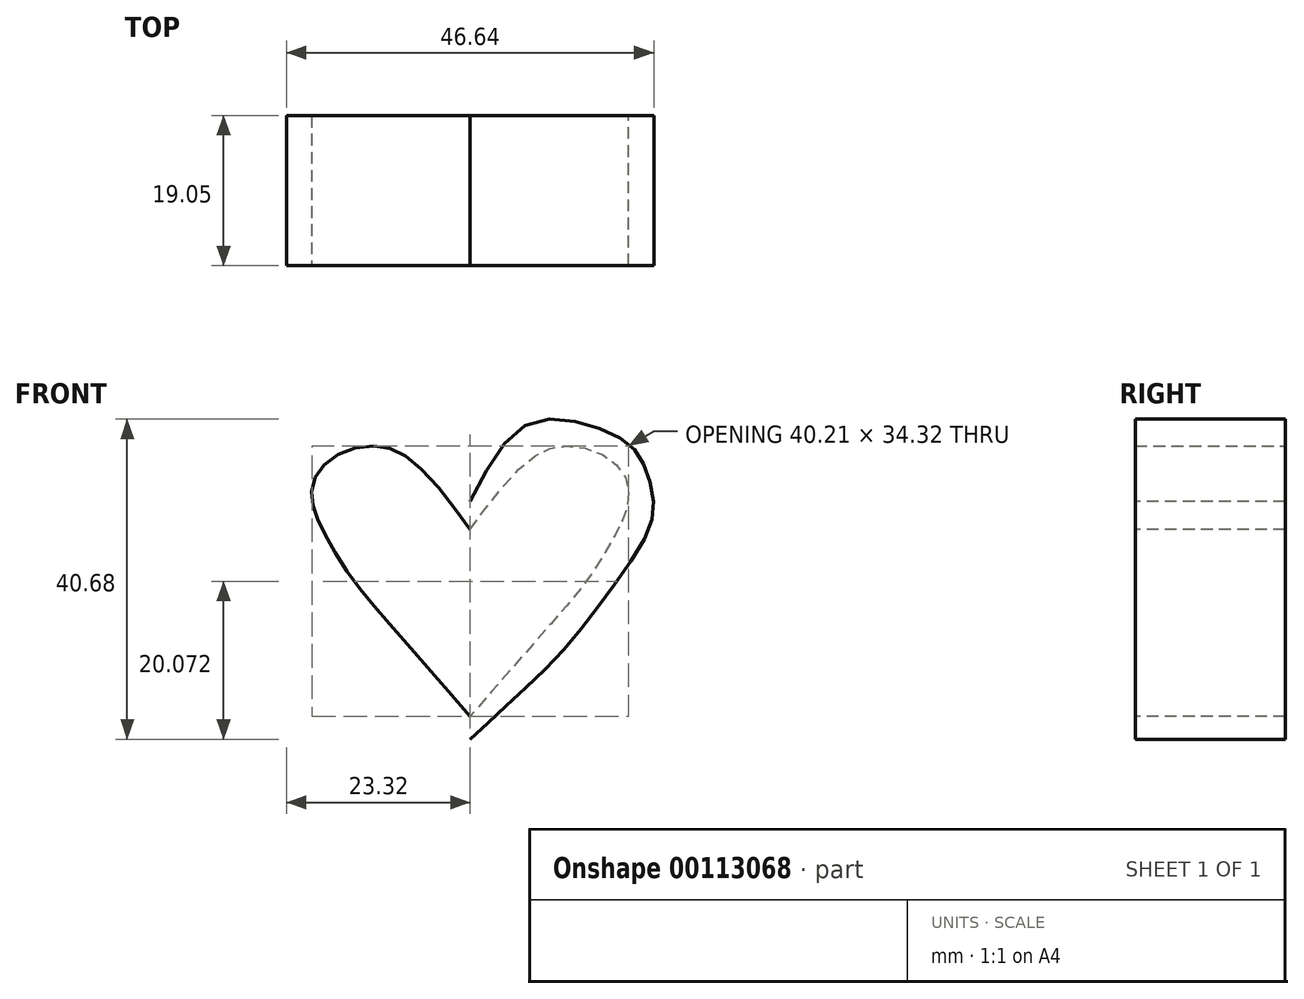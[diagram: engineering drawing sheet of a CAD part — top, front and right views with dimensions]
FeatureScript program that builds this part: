
annotation { "Feature Type Name" : "Feature", "Feature Type Description" : "" }
export const myFeature = defineFeature(function(context is Context, id is Id, definition is map)
    precondition{}
    {
        {
            var Q0;
            Q0=qCreatedBy(makeId("Front.planeOp"),FACE);
            var sketch = newSketch(context, id + "F0", { "sketchPlane" : qUnion([Q0])});
            skFitSpline(sketch, "E0", {"points": [v(0, 0) * mm, v(6.95, 9.63) * mm, v(14.55, 9.86) * mm, v(20.08, 7.33) * mm, v(22.15, 4.45) * mm, v(23.3, 0) * mm, v(22.38, -4.3) * mm, v(17.31, -11.9) * mm, v(11.78, -18.93) * mm, v(5.45, -25.15) * mm, v(0, -30.21) * mm], "startDerivative": vector(47.19, 93.17) * mm, "endDerivative": vector(-51.53, -48) * mm});
            skFitSpline(sketch, "E1.MirrorCS", {"points": [v(0, 0) * mm, v(-6.95, 9.63) * mm, v(-14.55, 9.86) * mm, v(-20.08, 7.33) * mm, v(-22.15, 4.45) * mm, v(-23.3, 0) * mm, v(-22.38, -4.3) * mm, v(-17.31, -11.9) * mm, v(-11.78, -18.93) * mm, v(-5.45, -25.15) * mm, v(0, -30.21) * mm], "startDerivative": vector(-47.19, 93.17) * mm, "endDerivative": vector(51.53, -48) * mm});
            skSolve(sketch);
        }
        {
            var Q0;
            Q0 = qSketchRegion(id + "F0", true);
            extrude(context, id + "F1", {"entities" : qUnion([Q0]), "oppositeDirection" : true, "depth" : 19.05 * mm});
        }
        {
            var Q0;
            Q0=qCreatedBy(makeId("Front.planeOp"),FACE);
            var sketch = newSketch(context, id + "F2", { "sketchPlane" : qUnion([Q0])});
            skFitSpline(sketch, "E2", {"points": [v(0, -3.56) * mm, v(6.76, 4.62) * mm, v(11.2, 6.97) * mm, v(16.33, 6.18) * mm, v(19.63, 3.23) * mm, v(20.07, 0) * mm, v(18.94, -3.2) * mm, v(15.28, -9.38) * mm, v(10.07, -15.73) * mm, v(0, -27.3) * mm], "startDerivative": vector(39.07, 56.91) * mm, "endDerivative": vector(-62.75, -72.4) * mm});
            skFitSpline(sketch, "E3.MirrorCS", {"points": [v(0, -3.56) * mm, v(-6.76, 4.62) * mm, v(-11.2, 6.97) * mm, v(-16.33, 6.18) * mm, v(-19.63, 3.23) * mm, v(-20.07, 0) * mm, v(-18.94, -3.2) * mm, v(-15.28, -9.38) * mm, v(-10.07, -15.73) * mm, v(0, -27.3) * mm], "startDerivative": vector(-39.07, 56.91) * mm, "endDerivative": vector(62.75, -72.4) * mm});
            skSolve(sketch);
        }
        {
            var Q0;
            Q0 = qSketchRegion(id + "F2", true);
            extrude(context, id + "F3", {"entities" : qUnion([Q0]), "operationType" : NewBodyOperationType.REMOVE, "oppositeDirection" : true, "depth" : 19.05 * mm});
        }
    });
